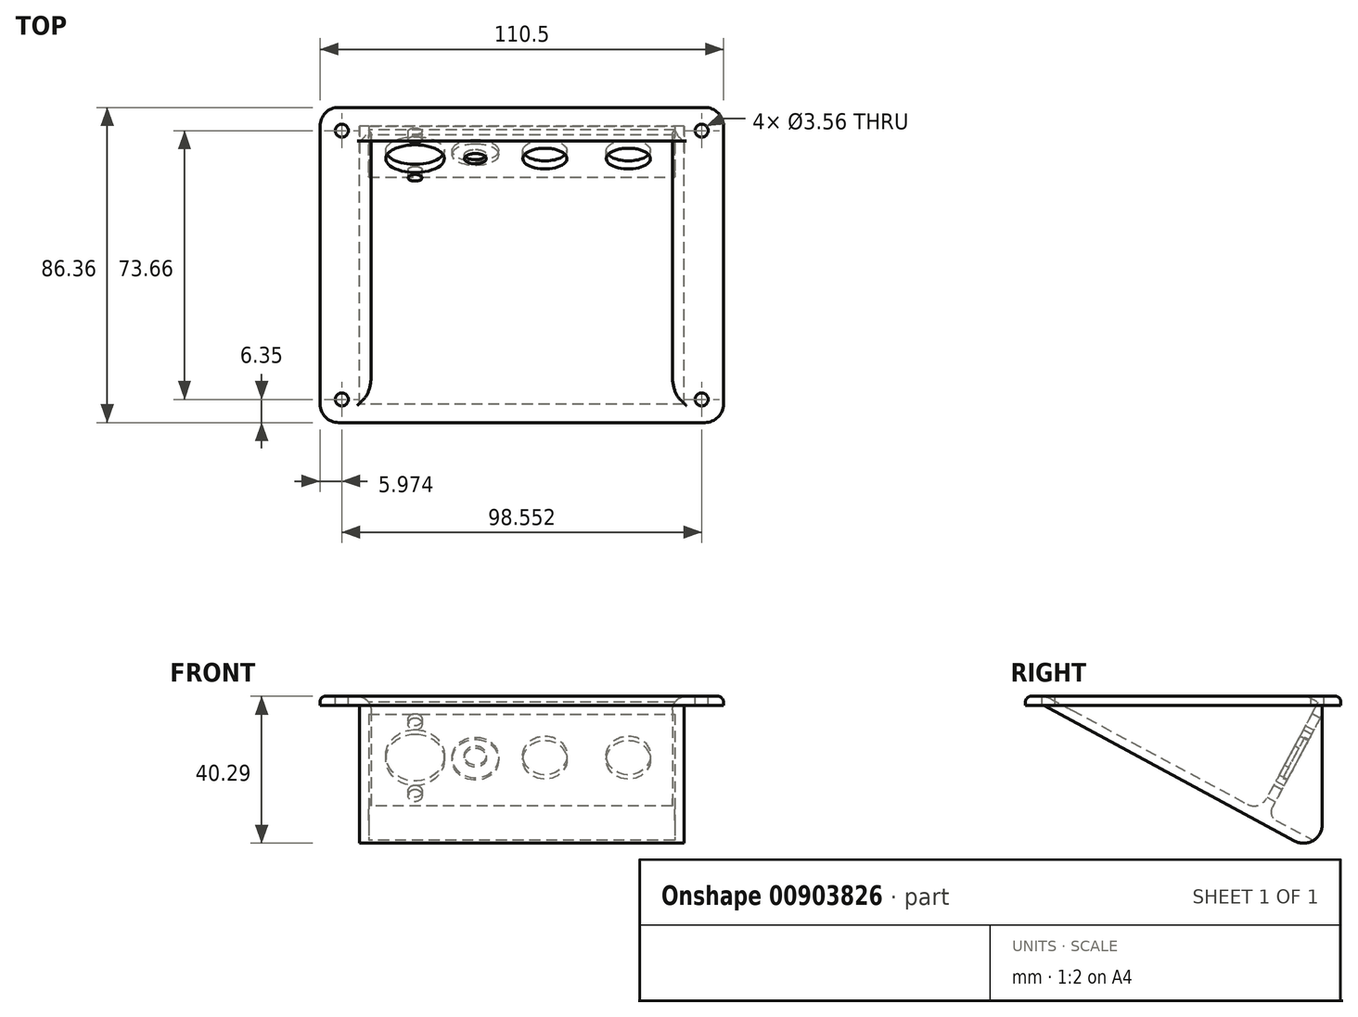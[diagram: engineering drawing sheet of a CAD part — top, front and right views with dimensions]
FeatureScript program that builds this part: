
annotation { "Feature Type Name" : "Feature", "Feature Type Description" : "" }
export const myFeature = defineFeature(function(context is Context, id is Id, definition is map)
    precondition{}
    {
        {
            var Q0;
            Q0=qCreatedBy(makeId("Top.planeOp"),FACE);
            var sketch = newSketch(context, id + "F0", { "sketchPlane" : qUnion([Q0])});
            skLineSegment(sketch, "E0.bottom", {"start": v(44.45, -38.1) * mm, "end": v(-44.45, -38.1) * mm});
            skLineSegment(sketch, "E0.top", {"start": v(44.45, 38.1) * mm, "end": v(-44.45, 38.1) * mm});
            skLineSegment(sketch, "E0.left", {"start": v(44.45, -38.1) * mm, "end": v(44.45, 38.1) * mm});
            skLineSegment(sketch, "E0.right", {"start": v(-44.45, -38.1) * mm, "end": v(-44.45, 38.1) * mm});
            skPoint(sketch, "E0.middle", {"position": v(0, 0) * mm});
            skSolve(sketch);
        }
        {
            var Q0;
            Q0 = qSketchRegion(id + "F0", true);
            extrude(context, id + "F1", {"entities" : qUnion([Q0]), "depth" : 50.8 * mm, "offsetDistance" : 25.4 * mm});
        }
        {
            var Q0;
            Q0=makeQuery(id+"F1.opExtrude","SWEPT_FACE",FACE,{"disambiguationData":[OSD([sQuery(id+"F0.wireOp",EDGE,"E0.right")])]});
            var sketch = newSketch(context, id + "F2", { "sketchPlane" : qUnion([Q0])});
            skLineSegment(sketch, "E1", {"start": v(38.1, 50.8) * mm, "end": v(-39.5, 8.86) * mm});
            skLineSegment(sketch, "E2", {"start": v(-39.5, 8.86) * mm, "end": v(-39.5, -2.37) * mm});
            skLineSegment(sketch, "E3", {"start": v(-39.5, -2.37) * mm, "end": v(38.16, -2.37) * mm});
            skLineSegment(sketch, "E4", {"start": v(38.16, -2.37) * mm, "end": v(38.1, 50.8) * mm});
            skSolve(sketch);
        }
        {
            var Q0;
            Q0 = qSketchRegion(id + "F2", true);
            extrude(context, id + "F3", {"entities" : qUnion([Q0]), "operationType" : NewBodyOperationType.REMOVE, "endBound" : BoundingType.THROUGH_ALL, "oppositeDirection" : true, "depth" : 25.4 * mm, "offsetDistance" : 25.4 * mm});
        }
        {
            var Q0;
            Q0=makeQuery(id+"F1.opExtrude","CAP_FACE",FACE,{"disambiguationData":[OSD([sQuery(id+"F0.wireOp",EDGE,"E0.bottom"),sQuery(id+"F0.wireOp",EDGE,"E0.top"),sQuery(id+"F0.wireOp",EDGE,"E0.left"),sQuery(id+"F0.wireOp",EDGE,"E0.right")])],"isStart":false});
            var sketch = newSketch(context, id + "F4", { "sketchPlane" : qUnion([Q0])});
            skLineSegment(sketch, "E5.bottom", {"start": v(55.25, -43.18) * mm, "end": v(-55.24, -43.18) * mm});
            skLineSegment(sketch, "E5.top", {"start": v(55.25, 43.18) * mm, "end": v(-55.25, 43.18) * mm});
            skLineSegment(sketch, "E5.left", {"start": v(55.25, -43.18) * mm, "end": v(55.24, 43.18) * mm});
            skLineSegment(sketch, "E5.right", {"start": v(-55.24, -43.18) * mm, "end": v(-55.25, 43.18) * mm});
            skPoint(sketch, "E5.middle", {"position": v(0, 0) * mm});
            skSolve(sketch);
        }
        {
            var Q0;
            Q0 = qSketchRegion(id + "F4", true);
            extrude(context, id + "F5", {"entities" : qUnion([Q0]), "operationType" : NewBodyOperationType.ADD, "depth" : 2.54 * mm, "offsetDistance" : 25.4 * mm});
        }
        {
            var Q0;
            Q0=qCreatedBy(makeId("Right.planeOp"),FACE);
            var sketch = newSketch(context, id + "F6", { "sketchPlane" : qUnion([Q0])});
            skLineSegment(sketch, "E6.bottom", {"start": v(-36.3, 91.03) * mm, "end": v(36.99, 51.74) * mm});
            skLineSegment(sketch, "E6.top", {"start": v(-52.29, 61.21) * mm, "end": v(21, 21.92) * mm});
            skLineSegment(sketch, "E6.left", {"start": v(-36.3, 91.03) * mm, "end": v(-52.29, 61.21) * mm});
            skLineSegment(sketch, "E6.right", {"start": v(36.99, 51.74) * mm, "end": v(21, 21.92) * mm});
            skSolve(sketch);
        }
        {
            var Q0;
            Q0 = qSketchRegion(id + "F6", true);
            extrude(context, id + "F7", {"entities" : qUnion([Q0]), "operationType" : NewBodyOperationType.REMOVE, "depth" : 82.55 * mm, "offsetDistance" : 25.4 * mm, "symmetric" : true});
        }
        {
            var Q0;
            Q0=makeQuery(id+"F1.opExtrude","SWEPT_FACE",FACE,{"disambiguationData":[OSD([sQuery(id+"F0.wireOp",EDGE,"E0.top")])]});
            shell(context, id + "F8", {"entities" : qUnion([Q0]), "thickness" : 2.54 * mm});
        }
        {
            var Q0;
            Q0=makeQuery(id+"F7.boolean.opBoolean","COPY",EDGE,{"derivedFrom":makeQuery(id+"F7.opExtrude","SWEPT_EDGE",EDGE,{"disambiguationData":[OSD([sQuery(id+"F6.wireOp",EDGE,"E6.top"),sQuery(id+"F6.wireOp",EDGE,"E6.right")])]})});
            var Q1;
            Q1=makeQuery(id+"F7.boolean.opBoolean","INTERSECT",EDGE,{"derivedFrom":[makeQuery(id+"F5.opExtrude","CAP_FACE",FACE,{"disambiguationData":[OSD([sQuery(id+"F4.wireOp",EDGE,"E5.bottom"),sQuery(id+"F4.wireOp",EDGE,"E5.top"),sQuery(id+"F4.wireOp",EDGE,"E5.left"),sQuery(id+"F4.wireOp",EDGE,"E5.right")])],"isStart":false}),makeQuery(id+"F7.opExtrude","SWEPT_FACE",FACE,{"disambiguationData":[OSD([sQuery(id+"F6.wireOp",EDGE,"E6.right")])]})]});
            var Q2;
            Q2=makeQuery(id+"F7.boolean.opBoolean","INTERSECT",EDGE,{"derivedFrom":[makeQuery(id+"F5.opExtrude","CAP_FACE",FACE,{"disambiguationData":[OSD([sQuery(id+"F4.wireOp",EDGE,"E5.bottom"),sQuery(id+"F4.wireOp",EDGE,"E5.top"),sQuery(id+"F4.wireOp",EDGE,"E5.left"),sQuery(id+"F4.wireOp",EDGE,"E5.right")])],"isStart":false}),makeQuery(id+"F7.opExtrude","CAP_FACE",FACE,{"disambiguationData":[OSD([sQuery(id+"F6.wireOp",EDGE,"E6.bottom"),sQuery(id+"F6.wireOp",EDGE,"E6.top"),sQuery(id+"F6.wireOp",EDGE,"E6.left"),sQuery(id+"F6.wireOp",EDGE,"E6.right")])],"isStart":true})]});
            var Q3;
            Q3=makeQuery(id+"F7.boolean.opBoolean","INTERSECT",EDGE,{"derivedFrom":[makeQuery(id+"F5.opExtrude","CAP_FACE",FACE,{"disambiguationData":[OSD([sQuery(id+"F4.wireOp",EDGE,"E5.bottom"),sQuery(id+"F4.wireOp",EDGE,"E5.top"),sQuery(id+"F4.wireOp",EDGE,"E5.left"),sQuery(id+"F4.wireOp",EDGE,"E5.right")])],"isStart":false}),makeQuery(id+"F7.opExtrude","SWEPT_FACE",FACE,{"disambiguationData":[OSD([sQuery(id+"F6.wireOp",EDGE,"E6.top")])]})]});
            var Q4;
            Q4=makeQuery(id+"F7.boolean.opBoolean","INTERSECT",EDGE,{"derivedFrom":[makeQuery(id+"F5.opExtrude","CAP_FACE",FACE,{"disambiguationData":[OSD([sQuery(id+"F4.wireOp",EDGE,"E5.bottom"),sQuery(id+"F4.wireOp",EDGE,"E5.top"),sQuery(id+"F4.wireOp",EDGE,"E5.left"),sQuery(id+"F4.wireOp",EDGE,"E5.right")])],"isStart":false}),makeQuery(id+"F7.opExtrude","CAP_FACE",FACE,{"disambiguationData":[OSD([sQuery(id+"F6.wireOp",EDGE,"E6.bottom"),sQuery(id+"F6.wireOp",EDGE,"E6.top"),sQuery(id+"F6.wireOp",EDGE,"E6.left"),sQuery(id+"F6.wireOp",EDGE,"E6.right")])],"isStart":false})]});
            fillet(context, id + "F9", {"entities" : qUnion([Q0, Q1, Q2, Q3, Q4]), "tangentPropagation" : true, "radius" : 3.8 * mm, "defaultsChanged" : true, "vertexSettings" : [], "allowEdgeOverflow" : false});
        }
        {
            var Q0;
            Q0=makeQuery(id+"F5.opExtrude","SWEPT_EDGE",EDGE,{"disambiguationData":[OSD([sQuery(id+"F4.wireOp",EDGE,"E5.top"),sQuery(id+"F4.wireOp",EDGE,"E5.right")])]});
            var Q1;
            Q1=makeQuery(id+"F5.opExtrude","SWEPT_EDGE",EDGE,{"disambiguationData":[OSD([sQuery(id+"F4.wireOp",EDGE,"E5.top"),sQuery(id+"F4.wireOp",EDGE,"E5.left")])]});
            var Q2;
            Q2=makeQuery(id+"F5.opExtrude","SWEPT_EDGE",EDGE,{"disambiguationData":[OSD([sQuery(id+"F4.wireOp",EDGE,"E5.bottom"),sQuery(id+"F4.wireOp",EDGE,"E5.left")])]});
            var Q3;
            Q3=makeQuery(id+"F5.opExtrude","SWEPT_EDGE",EDGE,{"disambiguationData":[OSD([sQuery(id+"F4.wireOp",EDGE,"E5.bottom"),sQuery(id+"F4.wireOp",EDGE,"E5.right")])]});
            fillet(context, id + "F10", {"entities" : qUnion([Q0, Q1, Q2, Q3]), "tangentPropagation" : true, "radius" : 5.08 * mm, "defaultsChanged" : false, "vertexSettings" : [], "allowEdgeOverflow" : false});
        }
        {
            var Q0;
            Q0=makeQuery(id+"F8.opShell","OFFSET_FACE",FACE,{"disambiguationData":[OSD([sQuery(id+"F6.wireOp",EDGE,"E6.right")])]});
            var sketch = newSketch(context, id + "F11", { "sketchPlane" : qUnion([Q0])});
            skLineSegment(sketch, "E7", {"start": v(0, 46.5) * mm, "end": v(-29.21, 46.5) * mm, "construction": true});
            skCircle(sketch, "E8", {"center": v(-29.21, 46.5) * mm, "radius": 6.03 * mm});
            skCircle(sketch, "E9", {"center": v(-6.35, 46.5) * mm, "radius": 6.03 * mm});
            skPoint(sketch, "E10", {"position": v(-14.6, 46.5) * mm});
            skLineSegment(sketch, "E11", {"start": v(0, 46.5) * mm, "end": v(37.21, 46.5) * mm, "construction": true});
            skCircle(sketch, "E12", {"center": v(12.7, 46.5) * mm, "radius": 2.98 * mm});
            skCircle(sketch, "E13", {"center": v(29.21, 46.5) * mm, "radius": 8 * mm});
            skLineSegment(sketch, "E14", {"start": v(29.21, 46.5) * mm, "end": v(29.21, 57.6) * mm, "construction": true});
            skLineSegment(sketch, "E15", {"start": v(29.21, 46.5) * mm, "end": v(29.21, 35.38) * mm, "construction": true});
            skCircle(sketch, "E16", {"center": v(29.21, 57.6) * mm, "radius": 1.9 * mm});
            skCircle(sketch, "E17", {"center": v(29.21, 35.38) * mm, "radius": 1.9 * mm});
            skSolve(sketch);
        }
        {
            var Q0;
            Q0 = qSketchRegion(id + "F11", true);
            extrude(context, id + "F12", {"entities" : qUnion([Q0]), "operationType" : NewBodyOperationType.REMOVE, "endBound" : BoundingType.THROUGH_ALL, "oppositeDirection" : true, "depth" : 25.4 * mm, "offsetDistance" : 25.4 * mm});
        }
        {
            var Q0;
            Q0=makeQuery(id+"F3.boolean.opBoolean","INTERSECT",EDGE,{"derivedFrom":[makeQuery(id+"F1.opExtrude","SWEPT_FACE",FACE,{"disambiguationData":[OSD([sQuery(id+"F0.wireOp",EDGE,"E0.top")])]}),makeQuery(id+"F3.opExtrude","SWEPT_FACE",FACE,{"disambiguationData":[OSD([sQuery(id+"F2.wireOp",EDGE,"E1")])]})]});
            fillet(context, id + "F13", {"entities" : qUnion([Q0]), "tangentPropagation" : true, "radius" : 5.08 * mm, "defaultsChanged" : false, "vertexSettings" : [], "allowEdgeOverflow" : false});
        }
        {
            var Q0;
            Q0=makeQuery(id+"F8.opShell","TWEAK_EDGE",EDGE,{"derivedFrom":[makeQuery(id+"F3.boolean.opBoolean","COPY",FACE,{"derivedFrom":makeQuery(id+"F3.opExtrude","SWEPT_FACE",FACE,{"disambiguationData":[OSD([sQuery(id+"F2.wireOp",EDGE,"E1")])]})}),makeQuery(id+"F7.boolean.opBoolean","COPY",FACE,{"derivedFrom":makeQuery(id+"F7.opExtrude","SWEPT_FACE",FACE,{"disambiguationData":[OSD([sQuery(id+"F6.wireOp",EDGE,"E6.right")])]})})]});
            fillet(context, id + "F14", {"entities" : qUnion([Q0]), "tangentPropagation" : true, "radius" : 2.54 * mm, "defaultsChanged" : true, "vertexSettings" : [], "allowEdgeOverflow" : false});
        }
        {
            var Q0;
            Q0=makeQuery(id+"F5.opExtrude","CAP_FACE",FACE,{"disambiguationData":[OSD([sQuery(id+"F4.wireOp",EDGE,"E5.bottom"),sQuery(id+"F4.wireOp",EDGE,"E5.top"),sQuery(id+"F4.wireOp",EDGE,"E5.left"),sQuery(id+"F4.wireOp",EDGE,"E5.right")])],"isStart":false});
            var sketch = newSketch(context, id + "F15", { "sketchPlane" : qUnion([Q0])});
            skLineSegment(sketch, "E18", {"start": v(-49.28, 0) * mm, "end": v(-49.28, 36.83) * mm, "construction": true});
            skCircle(sketch, "E19", {"center": v(-49.28, 36.83) * mm, "radius": 1.78 * mm});
            skCircle(sketch, "E20.MirrorC", {"center": v(49.28, 36.83) * mm, "radius": 1.78 * mm});
            skCircle(sketch, "E21.MirrorC", {"center": v(-49.28, -36.83) * mm, "radius": 1.78 * mm});
            skCircle(sketch, "E22.MirrorC", {"center": v(49.28, -36.83) * mm, "radius": 1.78 * mm});
            skLineSegment(sketch, "E23", {"start": v(-49.28, 0) * mm, "end": v(0, 0) * mm, "construction": true});
            skSolve(sketch);
        }
        {
            var Q0;
            Q0 = qSketchRegion(id + "F15", true);
            extrude(context, id + "F16", {"entities" : qUnion([Q0]), "operationType" : NewBodyOperationType.REMOVE, "endBound" : BoundingType.THROUGH_ALL, "oppositeDirection" : true, "depth" : 25.4 * mm, "offsetDistance" : 25.4 * mm});
        }
        {
            var Q0;
            Q0=makeQuery(id+"F5.opExtrude","CAP_EDGE",EDGE,{"disambiguationData":[OSD([sQuery(id+"F4.wireOp",EDGE,"E5.bottom")])],"isStart":false});
            fillet(context, id + "F17", {"entities" : qUnion([Q0]), "tangentPropagation" : true, "radius" : 1.52 * mm, "defaultsChanged" : true, "vertexSettings" : [], "allowEdgeOverflow" : false});
        }
        {
            var Q0;
            Q0=makeQuery(id+"F8.opShell","OFFSET_FACE",FACE,{"disambiguationData":[OSD([sQuery(id+"F6.wireOp",EDGE,"E6.right")])]});
            var sketch = newSketch(context, id + "F18", { "sketchPlane" : qUnion([Q0])});
            skCircle(sketch, "E24", {"center": v(12.7, 46.5) * mm, "radius": 6.35 * mm});
            skSolve(sketch);
        }
        {
            var Q0;
            Q0 = qSketchRegion(id + "F18", true);
            extrude(context, id + "F19", {"entities" : qUnion([Q0]), "operationType" : NewBodyOperationType.REMOVE, "oppositeDirection" : true, "depth" : 1.27 * mm, "offsetDistance" : 25.4 * mm});
        }
    });
